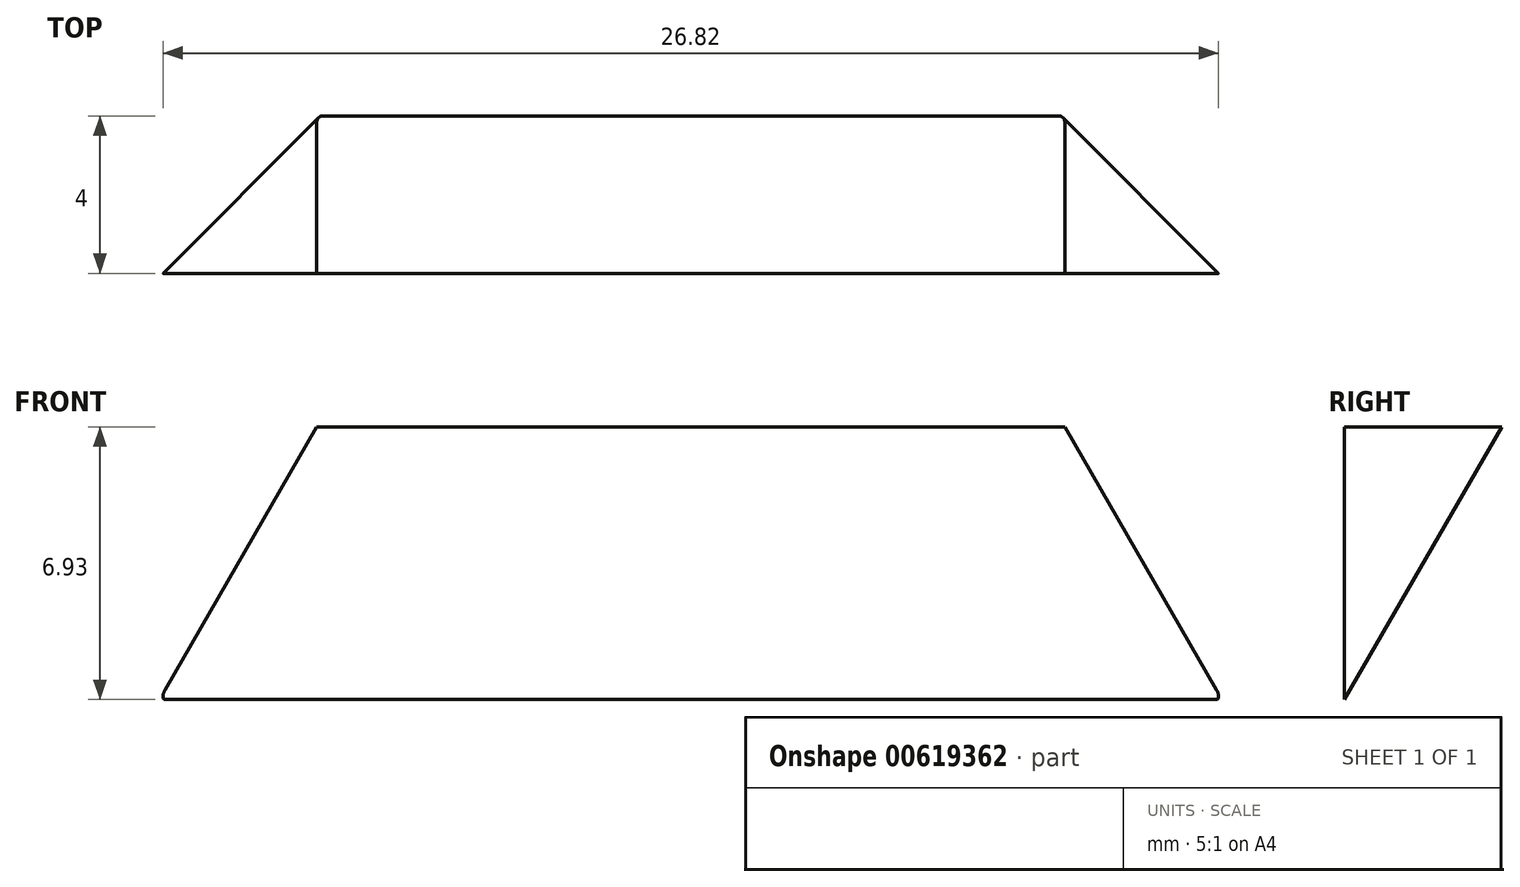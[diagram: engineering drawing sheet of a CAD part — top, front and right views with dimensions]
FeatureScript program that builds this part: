
annotation { "Feature Type Name" : "Feature", "Feature Type Description" : "" }
export const myFeature = defineFeature(function(context is Context, id is Id, definition is map)
    precondition{}
    {
        {
            assignVariable(context, id + "F0", {"name" : "x1", "anyValue" : 10});
        }
        {
            assignVariable(context, id + "F1", {"name" : "filletr", "anyValue" : .1});
        }
        {
            assignVariable(context, id + "F2", {"name" : "slotwidth", "anyValue" : 2});
        }
        {
            assignVariable(context, id + "F3", {"name" : "sliderlength", "anyValue" : (getVariable(context, 'x1') - getVariable(context, 'slotwidth')) / 2});
        }
        {
            assignVariable(context, id + "F4", {"name" : "holedepth", "anyValue" : .5});
        }
        {
            var Q0;
            Q0=qCreatedBy(makeId("Front.planeOp"),FACE);
            var sketch = newSketch(context, id + "F5", { "sketchPlane" : qUnion([Q0])});
            skLineSegment(sketch, "E0", {"start": v(9.5, 9) * mm, "end": v(14.7, 0) * mm});
            skLineSegment(sketch, "E1", {"start": v(14.7, 0) * mm, "end": v(-14.7, 0) * mm});
            skLineSegment(sketch, "E2", {"start": v(-14.7, 0) * mm, "end": v(-9.5, 9) * mm});
            skLineSegment(sketch, "E3", {"start": v(-9.5, 9) * mm, "end": v(9.5, 9) * mm});
            skLineSegment(sketch, "E4", {"start": v(0, 0) * mm, "end": v(0, 29.38) * mm, "construction": true});
            skSolve(sketch);
        }
        {
            var Q0;
            Q0=makeQuery(id+"F5.imprint","IMPRINT",FACE,{"disambiguationData":[TD([[makeQuery(id+"F5.imprint","IMPRINT",EDGE,{"derivedFrom":sQuery(id+"F5.wireOp",EDGE,"E0")}),-1.0]])]});
            extrude(context, id + "F6", {"entities" : qUnion([Q0]), "depth" : (getVariable(context, 'sliderlength')) * mm, "offsetDistance" : 25 * mm});
        }
        {
            var Q0;
            Q0=makeQuery(id+"F6.opExtrude","SWEPT_FACE",FACE,{"disambiguationData":[OSD([sQuery(id+"F5.wireOp",EDGE,"E3")])]});
            var sketch = newSketch(context, id + "F7", { "sketchPlane" : qUnion([Q0])});
            skLineSegment(sketch, "E5", {"start": v(-9.5, -20) * mm, "end": v(9.5, -20) * mm, "construction": true});
            skLineSegment(sketch, "E6", {"start": v(0, 0) * mm, "end": v(0, -40) * mm, "construction": true});
            skPoint(sketch, "E7", {"position": v(0, -20) * mm});
            skCircle(sketch, "E8", {"center": v(0, -20) * mm, "radius": 2.5 * mm});
            skSolve(sketch);
        }
        {
            var Q0;
            Q0=makeQuery(id+"F7.imprint","IMPRINT",FACE,{"disambiguationData":[TD([[makeQuery(id+"F7.imprint","IMPRINT",EDGE,{"derivedFrom":sQuery(id+"F7.wireOp",EDGE,"E8")}),1.0]])]});
            extrude(context, id + "F8", {"entities" : qUnion([Q0]), "operationType" : NewBodyOperationType.REMOVE, "oppositeDirection" : true, "depth" : (getVariable(context, 'holedepth')) * mm, "offsetDistance" : 25 * mm});
        }
        {
            var Q0;
            Q0=qCreatedBy(makeId("Right.planeOp"),FACE);
            var sketch = newSketch(context, id + "F9", { "sketchPlane" : qUnion([Q0])});
            skLineSegment(sketch, "E9", {"start": v(0, 9) * mm, "end": v(0, 0) * mm});
            skLineSegment(sketch, "E10", {"start": v(0, 0) * mm, "end": v(-5.2, 0) * mm});
            skLineSegment(sketch, "E11", {"start": v(-5.2, 0) * mm, "end": v(0, 9) * mm});
            skLineSegment(sketch, "E12", {"start": v(-40, 9) * mm, "end": v(-40, 0) * mm});
            skLineSegment(sketch, "E13", {"start": v(-40, 0) * mm, "end": v(-34.8, 0) * mm});
            skLineSegment(sketch, "E14", {"start": v(-34.8, 0) * mm, "end": v(-40, 9) * mm});
            skSolve(sketch);
        }
        {
            var Q0;
            Q0 = qSketchRegion(id + "F9", true);
            extrude(context, id + "F10", {"entities" : qUnion([Q0]), "operationType" : NewBodyOperationType.REMOVE, "endBound" : BoundingType.THROUGH_ALL, "depth" : 100 * mm, "offsetDistance" : 25 * mm, "hasSecondDirection" : true, "secondDirectionBound" : BoundingType.THROUGH_ALL, "secondDirectionOppositeDirection" : true, "secondDirectionDepth" : 25 * mm});
        }
        {
            var Q0;
            Q0=makeQuery(id+"F10.boolean.opBoolean","INTERSECT",EDGE,{"derivedFrom":[makeQuery(id+"F6.opExtrude","SWEPT_FACE",FACE,{"disambiguationData":[OSD([sQuery(id+"F5.wireOp",EDGE,"E2")])]}),makeQuery(id+"F10.opExtrude","SWEPT_FACE",FACE,{"disambiguationData":[OSD([sQuery(id+"F9.wireOp",EDGE,"E14")])]})]});
            var Q1;
            Q1=makeQuery(id+"F10.boolean.opBoolean","INTERSECT",EDGE,{"derivedFrom":[makeQuery(id+"F6.opExtrude","SWEPT_FACE",FACE,{"disambiguationData":[OSD([sQuery(id+"F5.wireOp",EDGE,"E0")])]}),makeQuery(id+"F10.opExtrude","SWEPT_FACE",FACE,{"disambiguationData":[OSD([sQuery(id+"F9.wireOp",EDGE,"E14")])]})]});
            var Q2;
            Q2=makeQuery(id+"F10.boolean.opBoolean","INTERSECT",EDGE,{"derivedFrom":[makeQuery(id+"F6.opExtrude","SWEPT_FACE",FACE,{"disambiguationData":[OSD([sQuery(id+"F5.wireOp",EDGE,"E0")])]}),makeQuery(id+"F10.opExtrude","SWEPT_FACE",FACE,{"disambiguationData":[OSD([sQuery(id+"F9.wireOp",EDGE,"E11")])]})]});
            var Q3;
            Q3=makeQuery(id+"F10.boolean.opBoolean","INTERSECT",EDGE,{"derivedFrom":[makeQuery(id+"F6.opExtrude","SWEPT_FACE",FACE,{"disambiguationData":[OSD([sQuery(id+"F5.wireOp",EDGE,"E2")])]}),makeQuery(id+"F10.opExtrude","SWEPT_FACE",FACE,{"disambiguationData":[OSD([sQuery(id+"F9.wireOp",EDGE,"E11")])]})]});
            fillet(context, id + "F11", {"entities" : qUnion([Q0, Q1, Q2, Q3]), "radius" : (getVariable(context, 'filletr')) * mm, "tangentPropagation" : true, "allowEdgeOverflow" : false});
        }
    });
